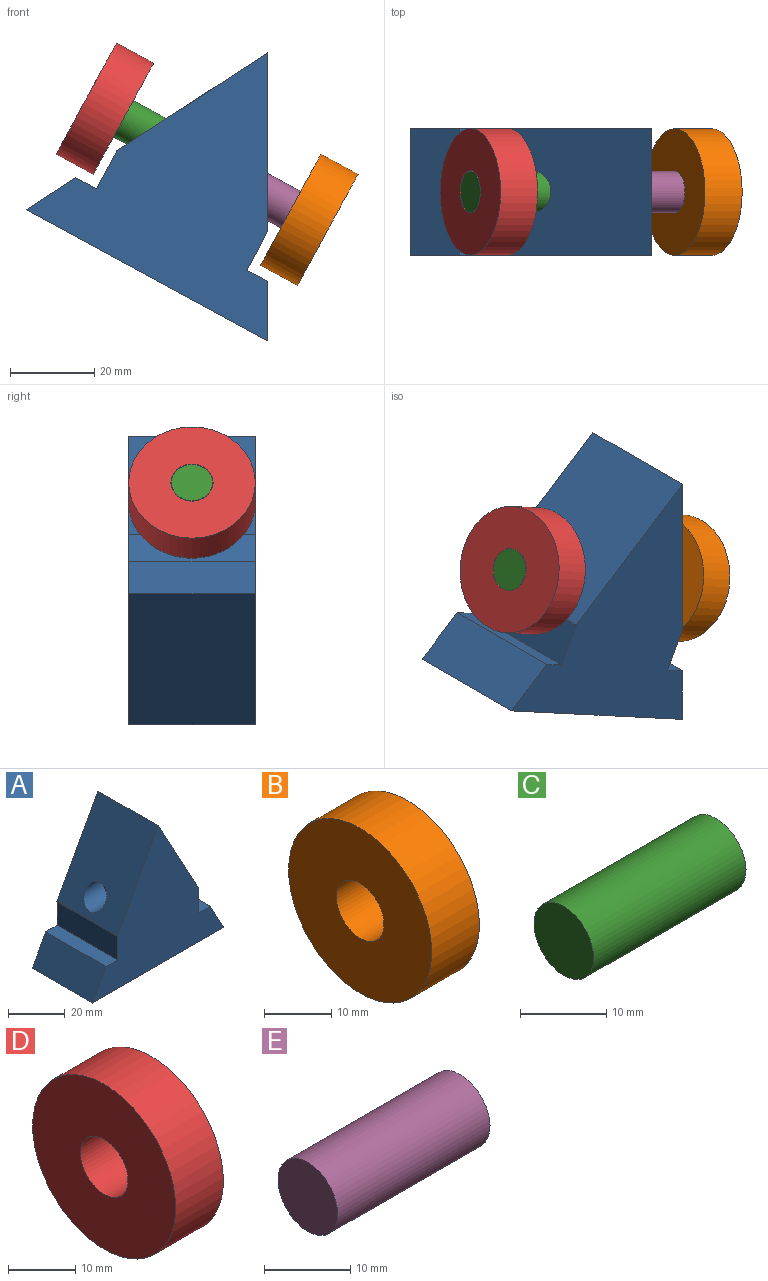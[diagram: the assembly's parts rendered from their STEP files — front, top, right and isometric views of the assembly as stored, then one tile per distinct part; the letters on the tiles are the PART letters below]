
ASSEMBLY  parts=5 mates=8
PART A: 16 faces, bbox 65.2x30x60 mm
  f0: plane 65.16x60mm, normal (0,1,0), area 1897.1mm2, adj f1,f3,f4,f5,f6,f11,f12,f13
  f1: plane 37.48x30mm, normal (-0.88,0,0.48), area 1190.1mm2, adj f0,f2,f4,f7,f13
  f2: plane 65.16x60mm, normal (0,-1,0), area 1897.1mm2, adj f1,f3,f4,f5,f6,f11,f12,f13
  f3: plane 30x12.42mm, normal (0.88,0,0.48), area 423.9mm2, adj f0,f2,f6,f11
  f4: plane 37.3x30mm, normal (0.88,0,0.48), area 1184mm2, adj f0,f1,f2,f9,f12
  f5: plane 30x12.33mm, normal (-0.88,0,0.48), area 421mm2, adj f0,f2,f6,f14
  f6: plane 65.16x30mm, normal (0,0,-1), area 1954.9mm2, adj f0,f2,f3,f5
  f7: cylinder r=5mm len=11.43mm, axis (-1,0,0), area 273.6mm2, adj f1,f8
  f8: plane 10x10mm, normal (-1,0,0), area 78.5mm2, adj f7
  f9: cylinder r=5mm len=11.43mm, axis (1,0,0), area 273.6mm2, adj f4,f10
  f10: plane 10x10mm, normal (1,0,0), area 78.5mm2, adj f9
  f11: plane 30x5.58mm, normal (0,0,1), area 167.5mm2, adj f0,f2,f3,f12
  f12: plane 30x10.28mm, normal (1,0,0), area 308.5mm2, adj f0,f2,f4,f11
  f13: plane 30x0.14mm, normal (0.86,0,-0.51), area 5mm2, adj f0,f1,f2,f15
  f14: plane 30x5.62mm, normal (0,0,1), area 168.5mm2, adj f0,f2,f5,f15
  f15: plane 30x10.33mm, normal (-1,0,0), area 309.9mm2, adj f0,f2,f13,f14
PART B: 4 faces, bbox 10x30x30 mm
  f0: cylinder r=15mm len=30mm, axis (1,0,0), area 942.5mm2, adj f1,f2
  f1: plane 30x30mm, normal (-1,0,0), area 628.3mm2, adj f0,f3
  f2: plane 30x30mm, normal (1,0,0), area 628.3mm2, adj f0,f3
  f3: cylinder r=5mm len=10mm, axis (1,0,0), area 314.2mm2, adj f1,f2
PART C: 3 faces, bbox 25x9.8x9.8 mm
  f0: cylinder r=4.9mm len=25mm, axis (-1,0,0), area 769.7mm2, adj f1,f2
  f1: plane 9.8x9.8mm, normal (1,0,0), area 75.4mm2, adj f0
  f2: plane 9.8x9.8mm, normal (-1,0,0), area 75.4mm2, adj f0
PART D: 4 faces, bbox 10x30x30 mm
  f0: cylinder r=15mm len=30mm, axis (-1,0,0), area 942.5mm2, adj f1,f2
  f1: plane 30x30mm, normal (1,0,0), area 628.3mm2, adj f0,f3
  f2: plane 30x30mm, normal (-1,0,0), area 628.3mm2, adj f0,f3
  f3: cylinder r=5mm len=10mm, axis (-1,0,0), area 314.2mm2, adj f1,f2
PART E: 3 faces, bbox 25x9.8x9.8 mm
  f0: cylinder r=4.9mm len=25mm, axis (1,0,0), area 769.7mm2, adj f1,f2
  f1: plane 9.8x9.8mm, normal (-1,0,0), area 75.4mm2, adj f0
  f2: plane 9.8x9.8mm, normal (1,0,0), area 75.4mm2, adj f0
PLACE A rot(axis=(0,1,0),28.5deg) t=(-17.9,12.68,7.92)mm
PLACE B rot(axis=(0,1,0),28.5deg) t=(-39.87,12.68,19.85)mm
PLACE C rot(axis=(0,1,0),28.5deg) t=(-17.9,12.68,7.92)mm
PLACE D rot(axis=(0,1,0),28.5deg) t=(4.07,12.68,-4.01)mm
PLACE E rot(axis=(0,1,0),28.5deg) t=(-17.9,12.68,7.92)mm
MATE slider C.f0 <-> D.f3  axis (-0.88,0,0.48) through (-35.55,-2.32,17.5)mm
MATE fastened B.f3 <-> E.f0  axis (0.88,0,-0.48) through (10.73,-2.32,-7.63)mm
MATE fastened D.f3 <-> C.f0  axis (-0.88,0,0.48) through (-46.53,-2.32,23.47)mm
MATE slider A.f7 <-> C.f0  axis (-0.88,0,0.48) through (-34.66,-2.32,17.02)mm
MATE fastened E.f0 <-> A.f7  axis (0.88,0,-0.48) through (-11.24,-2.32,4.3)mm
MATE slider E.f0 <-> B.f3  axis (0.88,0,-0.48) through (10.73,-2.32,-7.63)mm
MATE fastened C.f0 <-> A.f7  axis (-0.88,0,0.48) through (-24.56,-2.32,11.54)mm
MATE parallel A.f4 <-> E.f0  axis (1,0,0) through (-3.58,-2.32,0.14)mm
